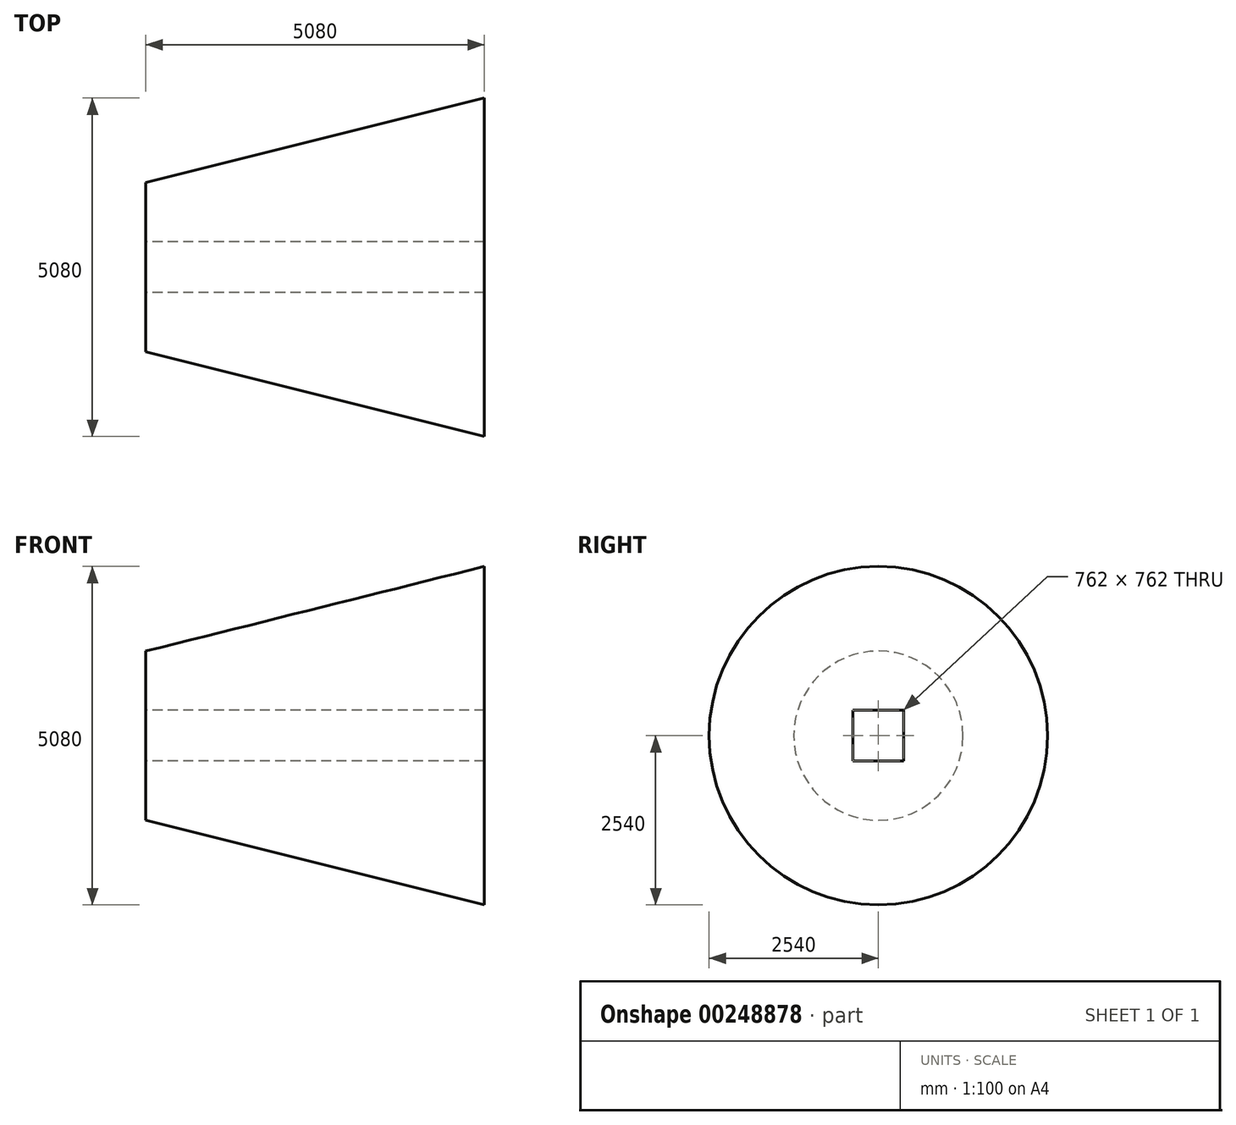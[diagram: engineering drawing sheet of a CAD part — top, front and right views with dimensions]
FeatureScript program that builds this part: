
annotation { "Feature Type Name" : "Feature", "Feature Type Description" : "" }
export const myFeature = defineFeature(function(context is Context, id is Id, definition is map)
    precondition{}
    {
        {
            var Q0;
            Q0=qCreatedBy(makeId("Front.planeOp"),FACE);
            var sketch = newSketch(context, id + "F0", { "sketchPlane" : qUnion([Q0])});
            skLineSegment(sketch, "E0", {"start": v(-414.8, 0) * mm, "end": v(5579.46, 0) * mm, "construction": true});
            skLineSegment(sketch, "E1", {"start": v(0, 0) * mm, "end": v(0, 1270) * mm});
            skLineSegment(sketch, "E2", {"start": v(0, 1270) * mm, "end": v(5080, 2540) * mm});
            skLineSegment(sketch, "E3", {"start": v(5080, 2540) * mm, "end": v(5080, 0) * mm});
            skLineSegment(sketch, "E4", {"start": v(5080, 0) * mm, "end": v(0, 0) * mm});
            skSolve(sketch);
        }
        {
            var Q0;
            Q0=makeQuery(id+"F0.imprint","IMPRINT",FACE,{"disambiguationData":[TD([[makeQuery(id+"F0.imprint","IMPRINT",EDGE,{"derivedFrom":sQuery(id+"F0.wireOp",EDGE,"E1")}),-1.0]])]});
            var Q1;
            Q1=sQuery(id+"F0.wireOp",EDGE,"E0");
            revolve(context, id + "F1", {"entities" : qUnion([Q0]), "axis" : qUnion([Q1]), "revolveType" : RevolveType.FULL});
        }
        {
            var Q0;
            Q0=makeQuery(id+"F1.opRevolve","SWEPT_FACE",FACE,{"disambiguationData":[OSD([sQuery(id+"F0.wireOp",EDGE,"E1")])]});
            var sketch = newSketch(context, id + "F2", { "sketchPlane" : qUnion([Q0])});
            skLineSegment(sketch, "E5.bottom", {"start": v(-381, -381) * mm, "end": v(381, -381) * mm});
            skLineSegment(sketch, "E5.top", {"start": v(-381, 381) * mm, "end": v(381, 381) * mm});
            skLineSegment(sketch, "E5.left", {"start": v(-381, -381) * mm, "end": v(-381, 381) * mm});
            skLineSegment(sketch, "E5.right", {"start": v(381, -381) * mm, "end": v(381, 381) * mm});
            skPoint(sketch, "E5.middle", {"position": v(0, 0) * mm});
            skSolve(sketch);
        }
        {
            var Q0;
            Q0 = qSketchRegion(id + "F2", true);
            extrude(context, id + "F3", {"entities" : qUnion([Q0]), "operationType" : NewBodyOperationType.REMOVE, "oppositeDirection" : true, "depth" : 5867.4 * mm});
        }
    });
